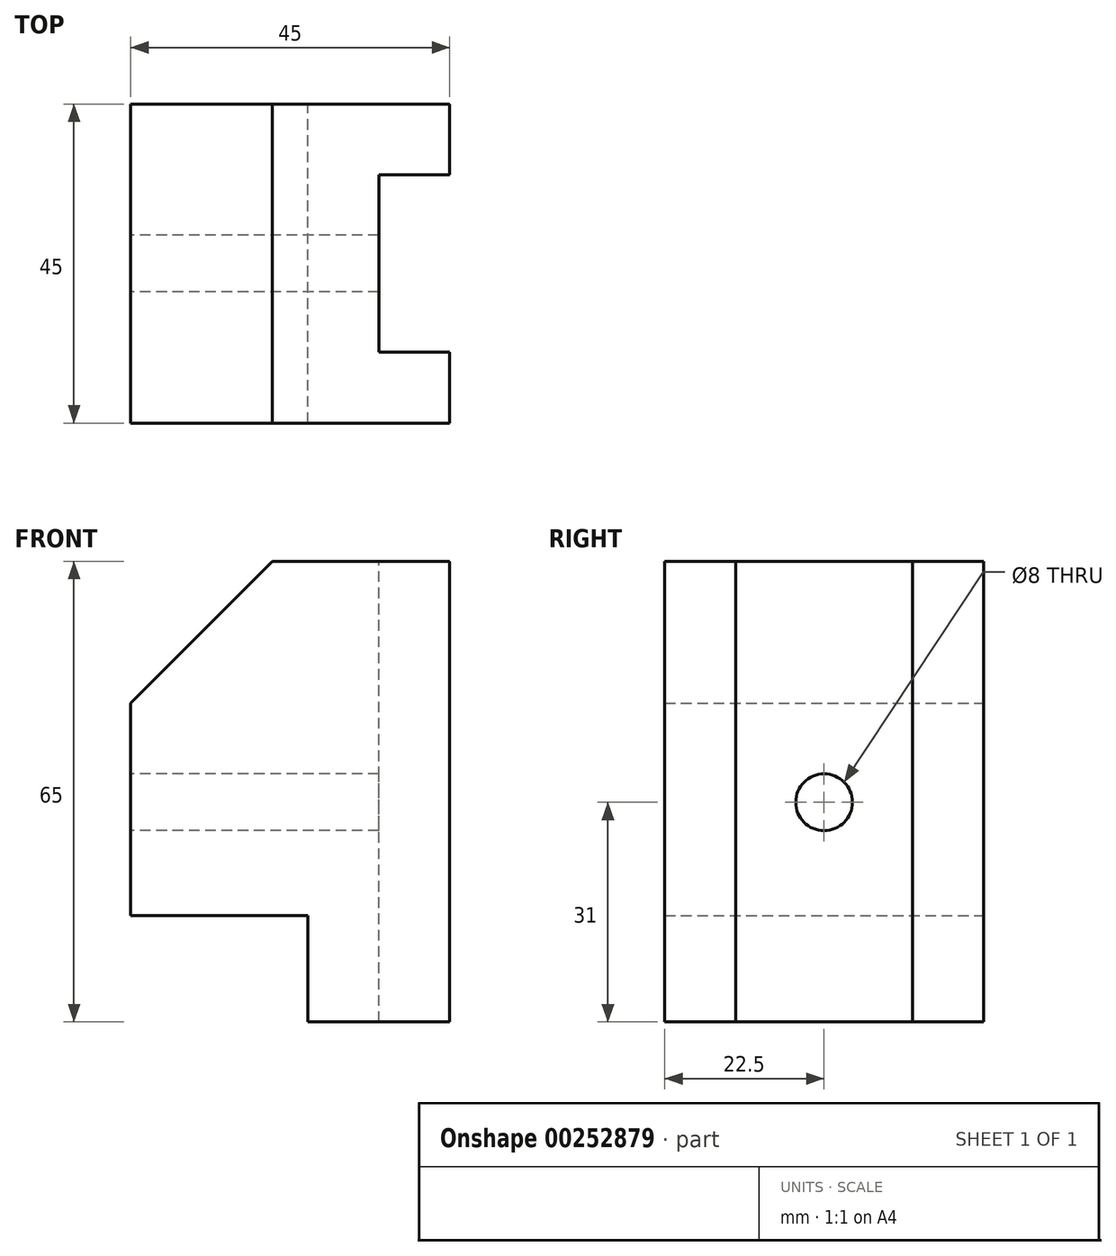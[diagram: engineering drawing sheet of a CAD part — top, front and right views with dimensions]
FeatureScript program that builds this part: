
annotation { "Feature Type Name" : "Feature", "Feature Type Description" : "" }
export const myFeature = defineFeature(function(context is Context, id is Id, definition is map)
    precondition{}
    {
        {
            var Q0;
            Q0=qCreatedBy(makeId("Front.planeOp"),FACE);
            var sketch = newSketch(context, id + "F0", { "sketchPlane" : qUnion([Q0])});
            skLineSegment(sketch, "E0", {"start": v(0, 0) * mm, "end": v(0, 65) * mm});
            skLineSegment(sketch, "E1", {"start": v(0, 65) * mm, "end": v(-45, 65) * mm});
            skLineSegment(sketch, "E2", {"start": v(-45, 65) * mm, "end": v(-45, 15) * mm});
            skLineSegment(sketch, "E3", {"start": v(-45, 15) * mm, "end": v(-20, 15) * mm});
            skLineSegment(sketch, "E4", {"start": v(-20, 15) * mm, "end": v(-20, 0) * mm});
            skLineSegment(sketch, "E5", {"start": v(-20, 0) * mm, "end": v(0, 0) * mm});
            skSolve(sketch);
        }
        {
            var Q0;
            Q0=makeQuery(id+"F0.imprint","IMPRINT",FACE,{"disambiguationData":[TD([[makeQuery(id+"F0.imprint","IMPRINT",EDGE,{"derivedFrom":sQuery(id+"F0.wireOp",EDGE,"E0")}),1.0]])]});
            extrude(context, id + "F1", {"entities" : qUnion([Q0]), "depth" : 45 * mm, "symmetric" : true});
        }
        {
            var Q0;
            Q0=makeQuery(id+"F1.opExtrude","SWEPT_EDGE",EDGE,{"disambiguationData":[OSD([sQuery(id+"F0.wireOp",EDGE,"E1"),sQuery(id+"F0.wireOp",EDGE,"E2")])]});
            chamfer(context, id + "F2", {"entities" : qUnion([Q0]), "width" : 20 * mm, "tangentPropagation" : true});
        }
        {
            var Q0;
            Q0=makeQuery(id+"F1.opExtrude","SWEPT_FACE",FACE,{"disambiguationData":[OSD([sQuery(id+"F0.wireOp",EDGE,"E1")])]});
            var sketch = newSketch(context, id + "F3", { "sketchPlane" : qUnion([Q0])});
            skLineSegment(sketch, "E6.bottom", {"start": v(10, -12.5) * mm, "end": v(-10, -12.5) * mm});
            skLineSegment(sketch, "E6.top", {"start": v(10, 12.5) * mm, "end": v(-10, 12.5) * mm});
            skLineSegment(sketch, "E6.left", {"start": v(10, -12.5) * mm, "end": v(10, 12.5) * mm});
            skLineSegment(sketch, "E6.right", {"start": v(-10, -12.5) * mm, "end": v(-10, 12.5) * mm});
            skPoint(sketch, "E6.middle", {"position": v(0, 0) * mm});
            skSolve(sketch);
        }
        {
            var Q0;
            {var subQ0=sQuery(id+"F3.wireOp",EDGE,"E6.right");Q0=makeQuery(id+"F3.imprint","IMPRINT",FACE,{"disambiguationData":[TD([[makeQuery(id+"F3.imprint","IMPRINT",EDGE,{"derivedFrom":subQ0}),-1.0]])]});}
            extrude(context, id + "F4", {"entities" : qUnion([Q0]), "operationType" : NewBodyOperationType.REMOVE, "endBound" : BoundingType.THROUGH_ALL, "oppositeDirection" : true, "depth" : 25 * mm});
        }
        {
            var Q0;
            Q0=makeQuery(id+"F1.opExtrude","SWEPT_FACE",FACE,{"disambiguationData":[OSD([sQuery(id+"F0.wireOp",EDGE,"E2")])]});
            var sketch = newSketch(context, id + "F5", { "sketchPlane" : qUnion([Q0])});
            skCircle(sketch, "E7", {"center": v(0, 31) * mm, "radius": 4 * mm});
            skSolve(sketch);
        }
        {
            var Q0;
            Q0=makeQuery(id+"F5.imprint","IMPRINT",FACE,{"disambiguationData":[TD([[makeQuery(id+"F5.imprint","IMPRINT",EDGE,{"derivedFrom":sQuery(id+"F5.wireOp",EDGE,"E7")}),1.0]])]});
            extrude(context, id + "F6", {"entities" : qUnion([Q0]), "operationType" : NewBodyOperationType.REMOVE, "endBound" : BoundingType.THROUGH_ALL, "oppositeDirection" : true, "depth" : 25 * mm});
        }
    });
